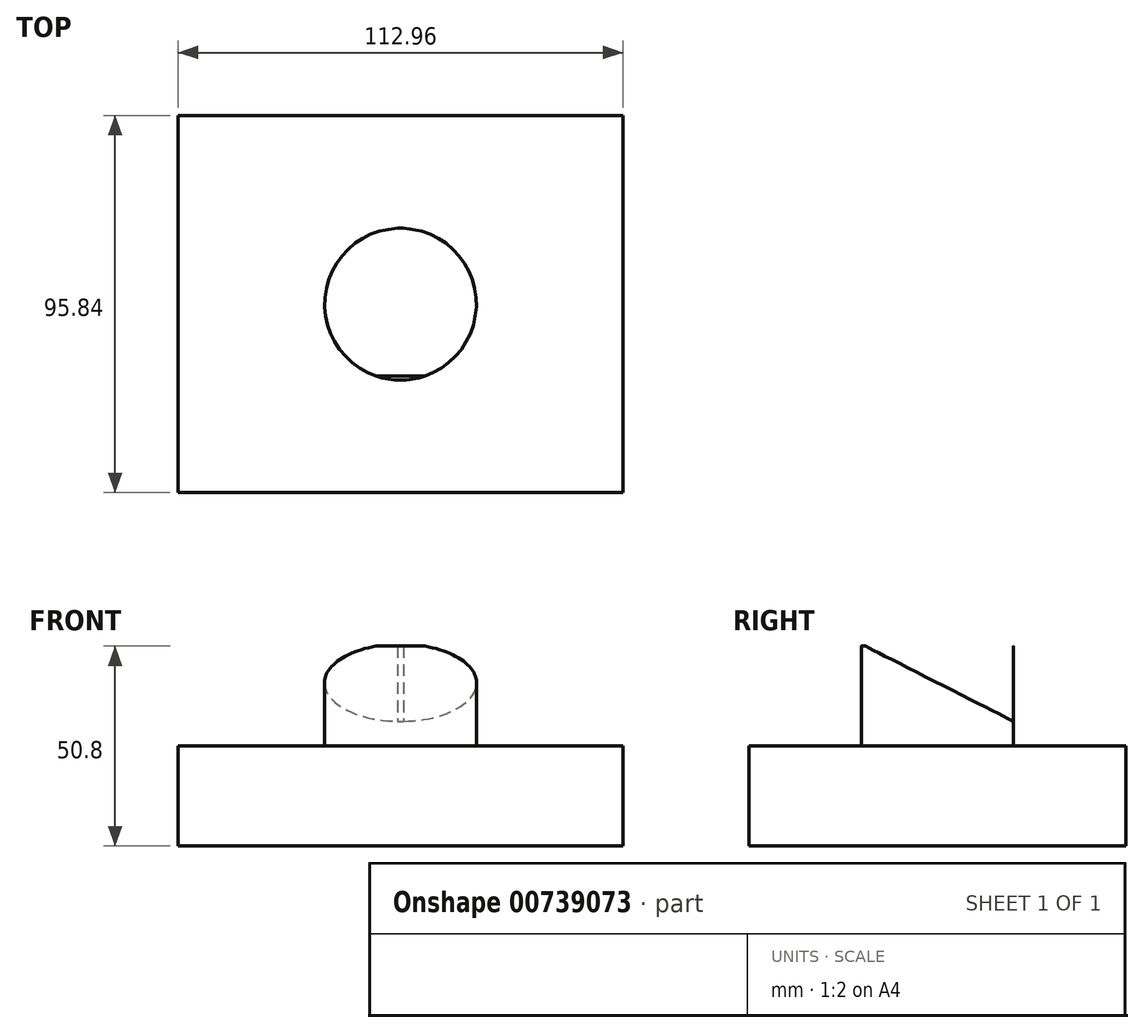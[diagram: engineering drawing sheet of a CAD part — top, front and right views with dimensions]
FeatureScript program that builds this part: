
annotation { "Feature Type Name" : "Feature", "Feature Type Description" : "" }
export const myFeature = defineFeature(function(context is Context, id is Id, definition is map)
    precondition{}
    {
        {
            var Q0;
            Q0=qCreatedBy(makeId("Top.planeOp"),FACE);
            var sketch = newSketch(context, id + "F0", { "sketchPlane" : qUnion([Q0])});
            skLineSegment(sketch, "E0.bottom", {"start": v(56.48, -47.92) * mm, "end": v(-56.48, -47.92) * mm});
            skLineSegment(sketch, "E0.top", {"start": v(56.48, 47.92) * mm, "end": v(-56.48, 47.92) * mm});
            skLineSegment(sketch, "E0.left", {"start": v(56.48, -47.92) * mm, "end": v(56.48, 47.92) * mm});
            skLineSegment(sketch, "E0.right", {"start": v(-56.48, -47.92) * mm, "end": v(-56.48, 47.92) * mm});
            skPoint(sketch, "E0.middle", {"position": v(0, 0) * mm});
            skSolve(sketch);
        }
        {
            var Q0;
            Q0 = qSketchRegion(id + "F0", true);
            extrude(context, id + "F1", {"entities" : qUnion([Q0]), "depth" : 25.4 * mm, "offsetDistance" : 25.4 * mm});
        }
        {
            var Q0;
            Q0=makeQuery(id+"F1.opExtrude","CAP_FACE",FACE,{"disambiguationData":[OSD([sQuery(id+"F0.wireOp",EDGE,"E0.bottom"),sQuery(id+"F0.wireOp",EDGE,"E0.top"),sQuery(id+"F0.wireOp",EDGE,"E0.left"),sQuery(id+"F0.wireOp",EDGE,"E0.right")])],"isStart":false});
            var sketch = newSketch(context, id + "F2", { "sketchPlane" : qUnion([Q0])});
            skCircle(sketch, "E1", {"center": v(0, 0) * mm, "radius": 19.33 * mm});
            skSolve(sketch);
        }
        {
            var Q0;
            Q0=makeQuery(id+"F2.imprint","IMPRINT",FACE,{"disambiguationData":[TD([[makeQuery(id+"F2.imprint","IMPRINT",EDGE,{"derivedFrom":sQuery(id+"F2.wireOp",EDGE,"E1")}),1.0]])]});
            extrude(context, id + "F3", {"entities" : qUnion([Q0]), "operationType" : NewBodyOperationType.ADD, "depth" : 25.4 * mm, "offsetDistance" : 25.4 * mm});
        }
        {
            var Q0;
            Q0=qCreatedBy(makeId("Right.planeOp"),FACE);
            var sketch = newSketch(context, id + "F4", { "sketchPlane" : qUnion([Q0])});
            skLineSegment(sketch, "E2", {"start": v(-19.3, 51.31) * mm, "end": v(19.3, 31.68) * mm});
            skLineSegment(sketch, "E3", {"start": v(19.3, 51.31) * mm, "end": v(19.3, 31.68) * mm});
            skLineSegment(sketch, "E4", {"start": v(19.3, 51.31) * mm, "end": v(-19.3, 51.31) * mm});
            skSolve(sketch);
        }
        {
            var Q0;
            Q0=makeQuery(id+"F4.imprint","IMPRINT",FACE,{"disambiguationData":[TD([[makeQuery(id+"F4.imprint","IMPRINT",EDGE,{"derivedFrom":sQuery(id+"F4.wireOp",EDGE,"E2")}),1.0]])]});
            var sketch = newSketch(context, id + "F5", { "sketchPlane" : qUnion([Q0])});
            skSolve(sketch);
        }
        {
            var Q0;
            Q0=makeQuery(id+"F5.imprint","IMPRINT",FACE,{"disambiguationData":[TD([[makeQuery(id+"F5.imprint","IMPRINT",EDGE,{"derivedFrom":makeQuery(id+"F4.imprint","IMPRINT",EDGE,{"derivedFrom":sQuery(id+"F4.wireOp",EDGE,"E2")})}),1.0]])]});
            var Q1;
            Q1=makeQuery(id+"F4.imprint","IMPRINT",FACE,{"disambiguationData":[TD([[makeQuery(id+"F4.imprint","IMPRINT",EDGE,{"derivedFrom":sQuery(id+"F4.wireOp",EDGE,"E2")}),1.0]])]});
            extrude(context, id + "F6", {"entities" : qUnion([Q0, Q1]), "operationType" : NewBodyOperationType.REMOVE, "oppositeDirection" : true, "depth" : 25.4 * mm, "offsetDistance" : 25.4 * mm, "hasSecondDirection" : true, "secondDirectionOppositeDirection" : false, "secondDirectionDepth" : 25.4 * mm});
        }
    });
